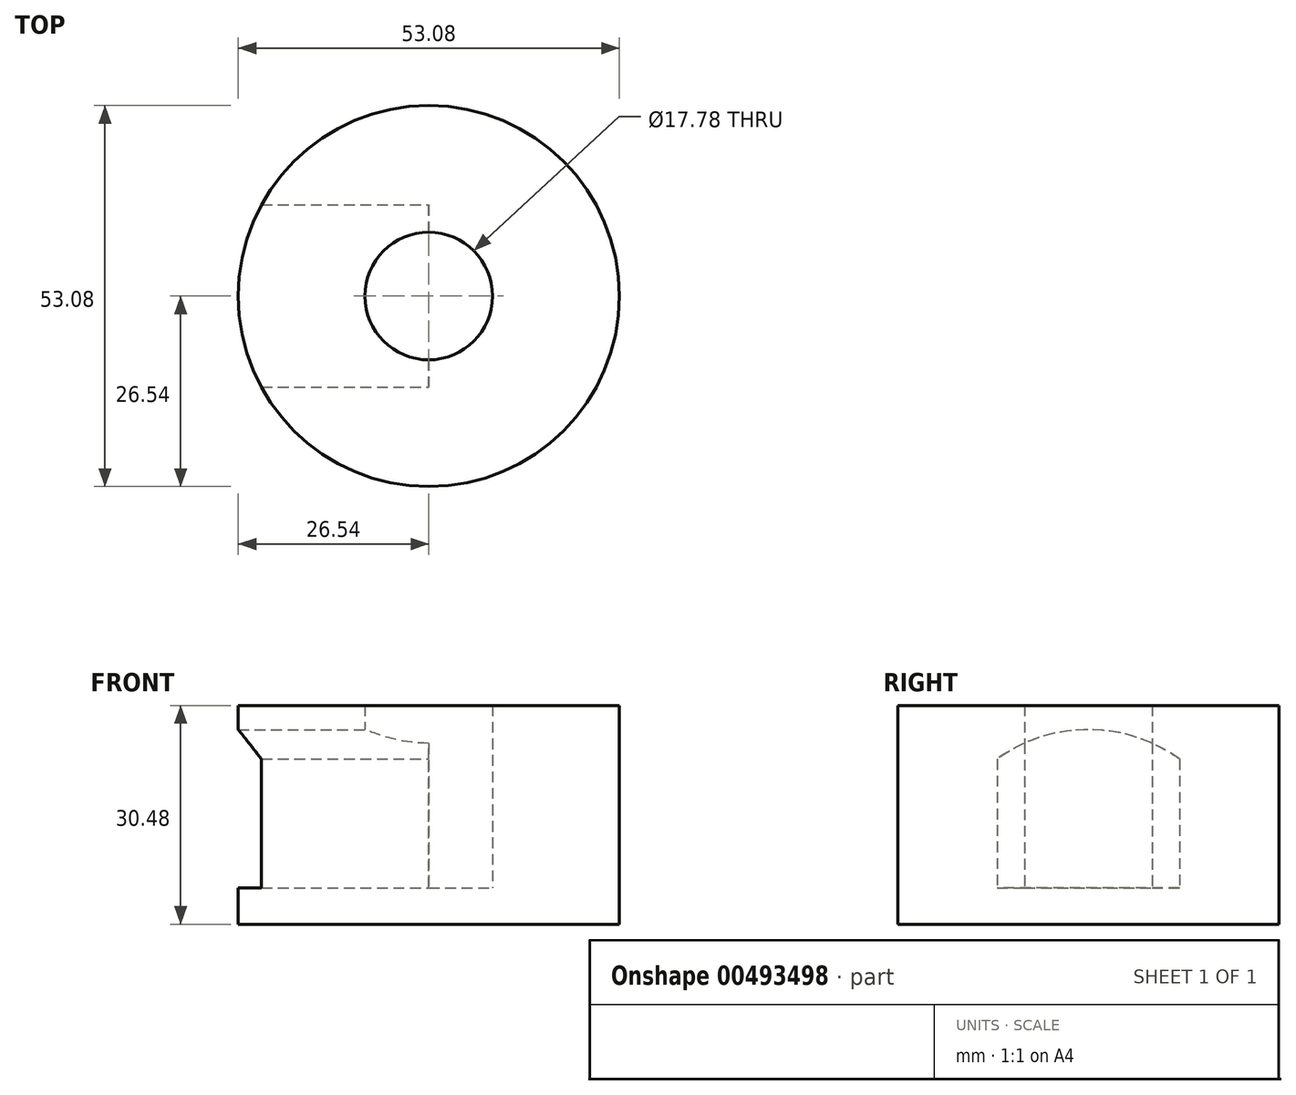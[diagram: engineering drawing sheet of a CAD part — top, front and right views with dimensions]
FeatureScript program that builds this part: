
annotation { "Feature Type Name" : "Feature", "Feature Type Description" : "" }
export const myFeature = defineFeature(function(context is Context, id is Id, definition is map)
    precondition{}
    {
        {
            var Q0;
            Q0=qCreatedBy(makeId("Top.planeOp"),FACE);
            var sketch = newSketch(context, id + "F0", { "sketchPlane" : qUnion([Q0])});
            skCircle(sketch, "E0", {"center": v(0, 0) * mm, "radius": 8.9 * mm});
            skCircle(sketch, "E1", {"center": v(0, 0) * mm, "radius": 26.54 * mm});
            skSolve(sketch);
        }
        {
            var Q0;
            Q0 = qSketchRegion(id + "F0", true);
            extrude(context, id + "F1", {"entities" : qUnion([Q0]), "depth" : 25.4 * mm, "offsetDistance" : 25.4 * mm});
        }
        {
            var Q0;
            Q0=qCreatedBy(makeId("Right.planeOp"),FACE);
            var sketch = newSketch(context, id + "F2", { "sketchPlane" : qUnion([Q0])});
            skLineSegment(sketch, "E2.0", {"start": v(-26.54, 0) * mm, "end": v(26.54, 0) * mm});
            skLineSegment(sketch, "E3", {"start": v(-12.7, 0) * mm, "end": v(12.7, 0) * mm});
            skLineSegment(sketch, "E4", {"start": v(-12.7, 0) * mm, "end": v(-12.7, 17.92) * mm});
            skLineSegment(sketch, "E5", {"start": v(12.7, 17.92) * mm, "end": v(12.7, 0) * mm});
            skArc(sketch, "E6", {"start": v(12.7, 17.92) * mm, "mid": v(0, 22.04) * mm, "end": v(-12.7, 17.92) * mm});
            skSolve(sketch);
        }
        {
            var Q0;
            Q0 = qSketchRegion(id + "F2", true);
            extrude(context, id + "F3", {"entities" : qUnion([Q0]), "operationType" : NewBodyOperationType.REMOVE, "oppositeDirection" : true, "depth" : 50.8 * mm, "offsetDistance" : 25.4 * mm});
        }
        {
            var Q0;
            Q0=makeQuery(id+"F1.opExtrude","CAP_FACE",FACE,{"disambiguationData":[OSD([sQuery(id+"F0.wireOp",EDGE,"E0"),sQuery(id+"F0.wireOp",EDGE,"E1")])],"isStart":true});
            var sketch = newSketch(context, id + "F4", { "sketchPlane" : qUnion([Q0])});
            skCircle(sketch, "E7.0.0", {"center": v(0, 0) * mm, "radius": 26.54 * mm});
            skSolve(sketch);
        }
        {
            var Q0;
            Q0 = qSketchRegion(id + "F4", true);
            extrude(context, id + "F5", {"entities" : qUnion([Q0]), "operationType" : NewBodyOperationType.ADD, "depth" : 5.08 * mm, "offsetDistance" : 25.4 * mm});
        }
    });
